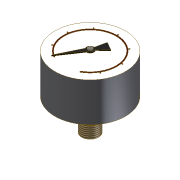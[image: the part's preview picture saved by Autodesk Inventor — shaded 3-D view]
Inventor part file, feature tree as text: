
AUTODESK INVENTOR PART (.ipt)
format: ipt  version: 2016 SP1 (Build 200210100, 210)  size: 161,280 bytes
history: native  units: mm
features: imported_body x1, thread x1
ambient origin geometry x8: Origin, YZ Plane, XZ Plane, XY Plane, X Axis, Y Axis, Z Axis, Center Point
bodies: Solid1 (feature_tree)
feature tree (2):
  imported_body  "Base1"
  thread  "Thread1"  [1 undecoded]
note: 1 required parameter value undecoded (feature->parameter linkage not recoverable at this tier; creation-order binding heuristic only, values carry confidence <= 0.55)
